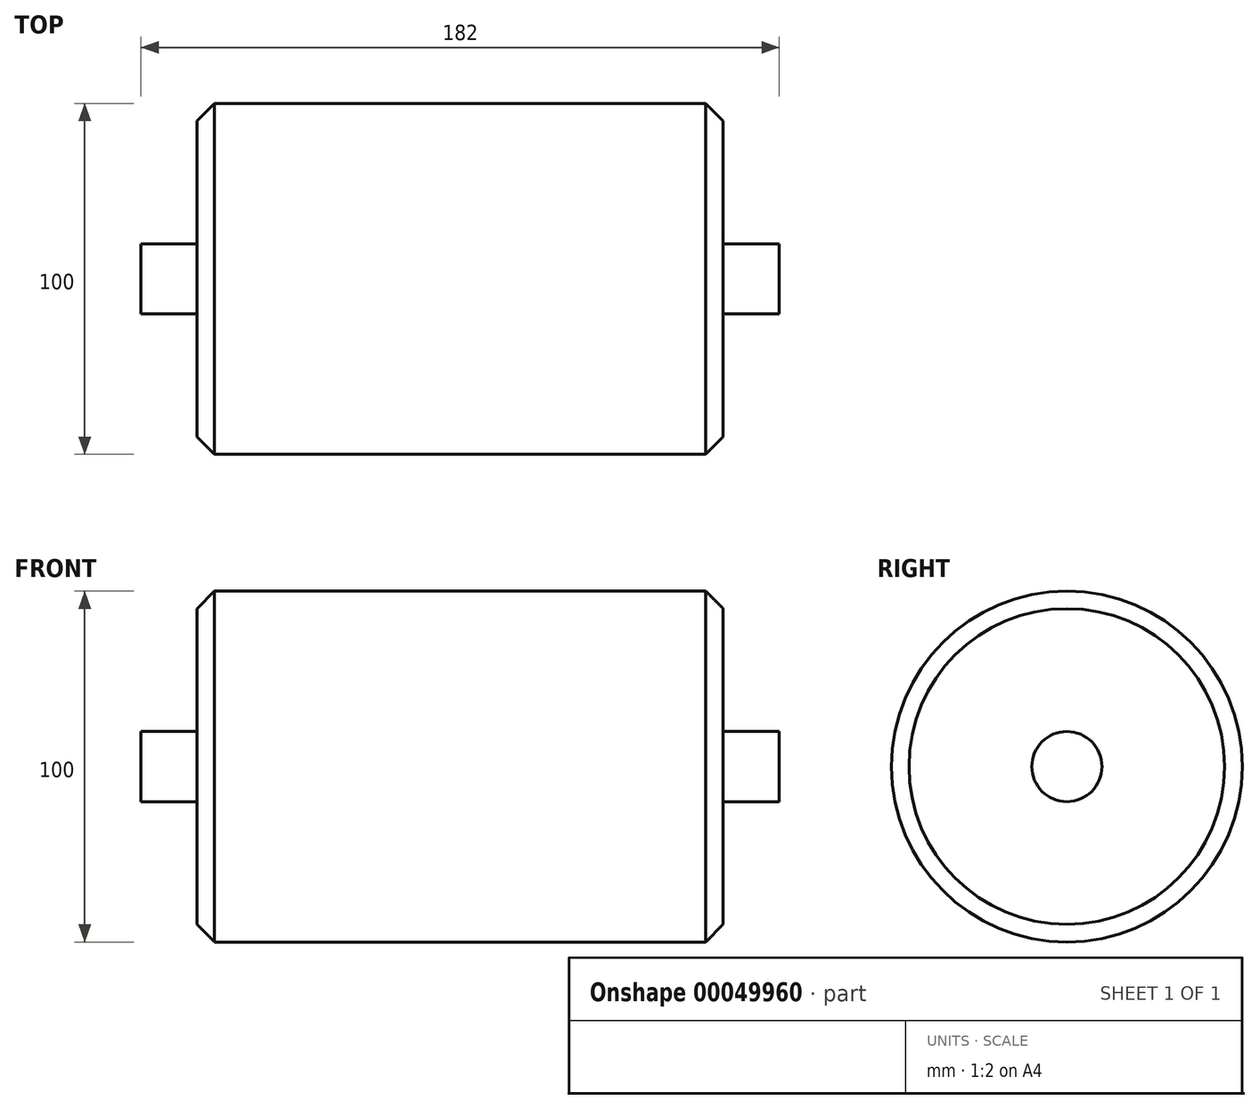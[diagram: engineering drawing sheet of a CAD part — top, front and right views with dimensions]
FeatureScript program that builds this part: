
annotation { "Feature Type Name" : "Feature", "Feature Type Description" : "" }
export const myFeature = defineFeature(function(context is Context, id is Id, definition is map)
    precondition{}
    {
        {
            var Q0;
            Q0=qCreatedBy(makeId("Front.planeOp"),FACE);
            var sketch = newSketch(context, id + "F0", { "sketchPlane" : qUnion([Q0])});
            skLineSegment(sketch, "E0", {"start": v(0, 0) * mm, "end": v(0, 10) * mm});
            skLineSegment(sketch, "E1", {"start": v(0, 10) * mm, "end": v(16, 10) * mm});
            skLineSegment(sketch, "E2", {"start": v(16, 10) * mm, "end": v(16, 50) * mm});
            skLineSegment(sketch, "E3", {"start": v(16, 50) * mm, "end": v(166, 50) * mm});
            skLineSegment(sketch, "E4", {"start": v(166, 50) * mm, "end": v(166, 10) * mm});
            skLineSegment(sketch, "E5", {"start": v(166, 10) * mm, "end": v(182, 10) * mm});
            skLineSegment(sketch, "E6", {"start": v(182, 10) * mm, "end": v(182, 0) * mm});
            skLineSegment(sketch, "E7", {"start": v(182, 0) * mm, "end": v(0, 0) * mm});
            skSolve(sketch);
        }
        {
            var Q0;
            Q0=makeQuery(id+"F0.imprint","IMPRINT",FACE,{"disambiguationData":[TD([[makeQuery(id+"F0.imprint","IMPRINT",EDGE,{"derivedFrom":sQuery(id+"F0.wireOp",EDGE,"E0")}),-1.0]])]});
            var Q1;
            Q1=sQuery(id+"F0.wireOp",EDGE,"E7");
            revolve(context, id + "F1", {"entities" : qUnion([Q0]), "axis" : qUnion([Q1]), "revolveType" : RevolveType.FULL});
        }
        {
            var Q0;
            Q0=makeQuery(id+"F1.opRevolve","SWEPT_EDGE",EDGE,{"disambiguationData":[OSD([sQuery(id+"F0.wireOp",EDGE,"E3"),sQuery(id+"F0.wireOp",EDGE,"E4")])]});
            chamfer(context, id + "F2", {"entities" : qUnion([Q0]), "chamferType" : ChamferType.OFFSET_ANGLE, "width" : 5 * mm, "oppositeDirection" : false, "angle" : 45 * degree, "tangentPropagation" : true});
        }
        {
            var Q0;
            Q0=makeQuery(id+"F1.opRevolve","SWEPT_EDGE",EDGE,{"disambiguationData":[OSD([sQuery(id+"F0.wireOp",EDGE,"E2"),sQuery(id+"F0.wireOp",EDGE,"E3")])]});
            chamfer(context, id + "F3", {"entities" : qUnion([Q0]), "chamferType" : ChamferType.OFFSET_ANGLE, "width" : 5 * mm, "oppositeDirection" : false, "angle" : 45 * degree, "tangentPropagation" : true});
        }
    });
